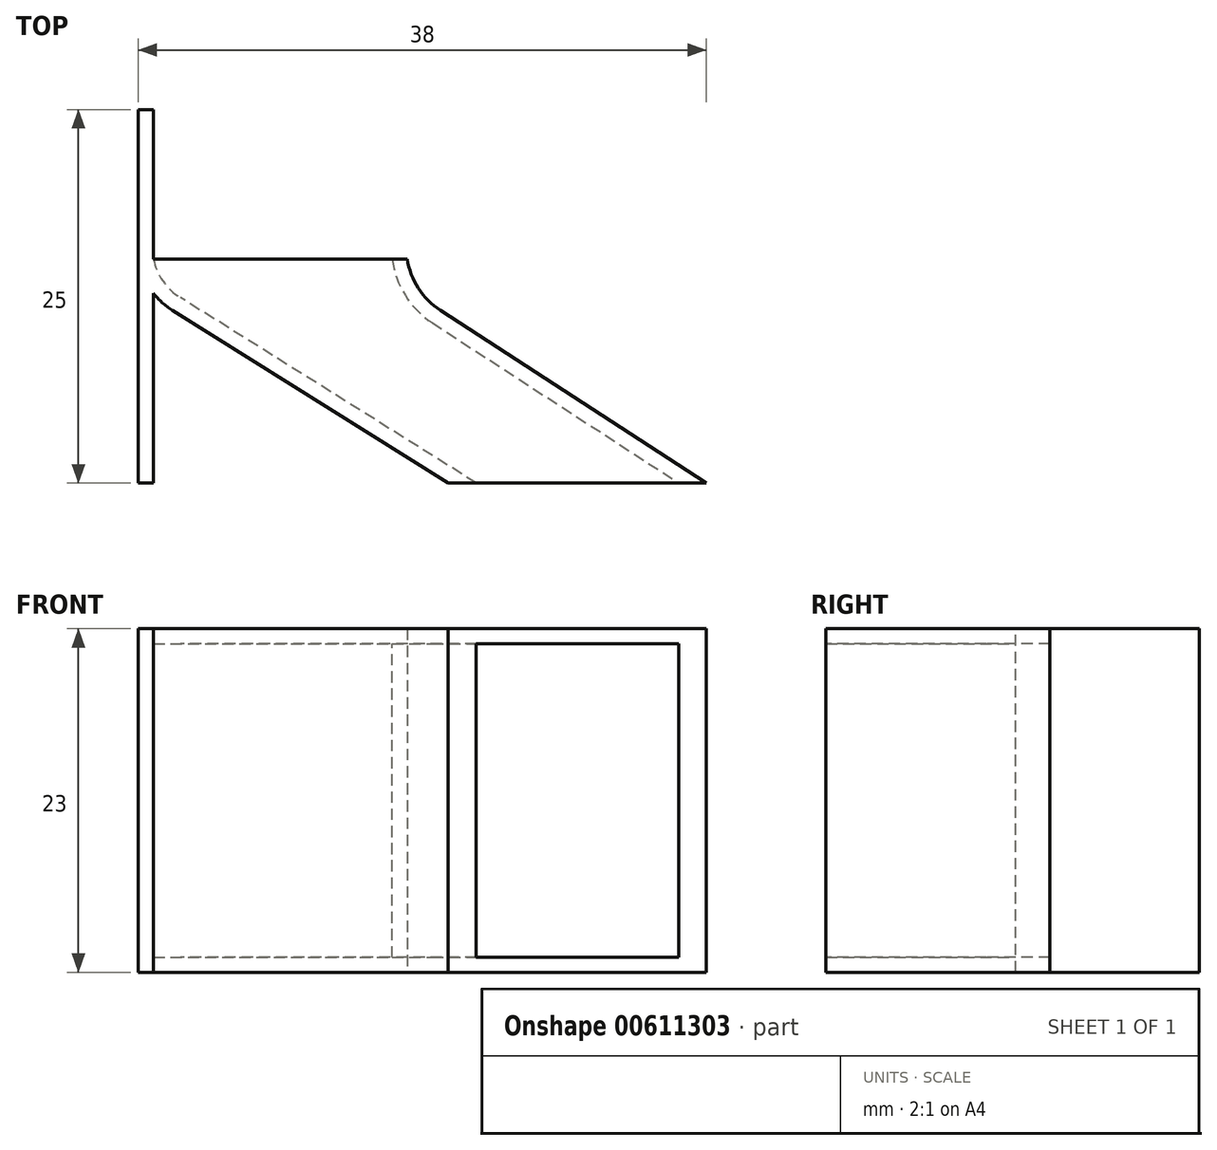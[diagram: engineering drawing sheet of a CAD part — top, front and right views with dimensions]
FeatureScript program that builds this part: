
annotation { "Feature Type Name" : "Feature", "Feature Type Description" : "" }
export const myFeature = defineFeature(function(context is Context, id is Id, definition is map)
    precondition{}
    {
        {
            var Q0;
            Q0=qCreatedBy(makeId("Top.planeOp"),FACE);
            var sketch = newSketch(context, id + "F0", { "sketchPlane" : qUnion([Q0])});
            skLineSegment(sketch, "E0.bottom", {"start": v(0, 0) * mm, "end": v(18, 0) * mm});
            skLineSegment(sketch, "E0.top", {"start": v(0, 2) * mm, "end": v(18, 2) * mm, "construction": true});
            skLineSegment(sketch, "E0.left", {"start": v(0, 0) * mm, "end": v(0, 2) * mm, "construction": true});
            skLineSegment(sketch, "E0.right", {"start": v(18, 0) * mm, "end": v(18, 2) * mm, "construction": true});
            skLineSegment(sketch, "E1.bottom", {"start": v(0, 0) * mm, "end": v(38, 0) * mm, "construction": true});
            skLineSegment(sketch, "E1.top", {"start": v(0, -13) * mm, "end": v(38, -13) * mm, "construction": true});
            skLineSegment(sketch, "E1.left", {"start": v(0, 0) * mm, "end": v(0, -13) * mm, "construction": true});
            skLineSegment(sketch, "E1.right", {"start": v(38, 0) * mm, "end": v(38, -13) * mm, "construction": true});
            skLineSegment(sketch, "E2", {"start": v(0, 2) * mm, "end": v(18, 2) * mm});
            skLineSegment(sketch, "E3", {"start": v(18, 0) * mm, "end": v(38, -13) * mm});
            skLineSegment(sketch, "E4", {"start": v(20.74, -13) * mm, "end": v(0, 0) * mm});
            skLineSegment(sketch, "E5", {"start": v(0, 2) * mm, "end": v(0, 0) * mm});
            skLineSegment(sketch, "E6", {"start": v(18, 2) * mm, "end": v(18, 0) * mm});
            skLineSegment(sketch, "E7", {"start": v(38, -13) * mm, "end": v(20.74, -13) * mm});
            skSolve(sketch);
        }
        {
            var Q0;
            Q0 = qSketchRegion(id + "F0", true);
            extrude(context, id + "F1", {"entities" : qUnion([Q0]), "depth" : 23 * mm, "offsetDistance" : 25 * mm});
        }
        {
            var Q0;
            Q0=makeQuery(id+"F1.opExtrude","SWEPT_EDGE",EDGE,{"disambiguationData":[OSD([sQuery(id+"F0.wireOp",EDGE,"E0.bottom"),sQuery(id+"F0.wireOp",EDGE,"E4"),sQuery(id+"F0.wireOp",EDGE,"E5")])]});
            fillet(context, id + "F2", {"entities" : qUnion([Q0]), "radius" : 5 * mm, "tangentPropagation" : true, "allowEdgeOverflow" : false});
        }
        {
            var Q0;
            Q0=makeQuery(id+"F1.opExtrude","SWEPT_EDGE",EDGE,{"disambiguationData":[OSD([sQuery(id+"F0.wireOp",EDGE,"E0.bottom"),sQuery(id+"F0.wireOp",EDGE,"E3"),sQuery(id+"F0.wireOp",EDGE,"E6")])]});
            fillet(context, id + "F3", {"entities" : qUnion([Q0]), "radius" : 5 * mm, "tangentPropagation" : true, "allowEdgeOverflow" : false});
        }
        {
            var Q0;
            Q0=makeQuery(id+"F1.opExtrude","SWEPT_FACE",FACE,{"disambiguationData":[OSD([sQuery(id+"F0.wireOp",EDGE,"E2")])]});
            var Q1;
            Q1=makeQuery(id+"F1.opExtrude","SWEPT_FACE",FACE,{"disambiguationData":[OSD([sQuery(id+"F0.wireOp",EDGE,"E7")])]});
            shell(context, id + "F4", {"entities" : qUnion([Q0, Q1]), "thickness" : 1 * mm});
        }
        {
            var Q0;
            Q0=makeQuery(id+"F1.opExtrude","SWEPT_FACE",FACE,{"disambiguationData":[OSD([sQuery(id+"F0.wireOp",EDGE,"E2")])]});
            var sketch = newSketch(context, id + "F5", { "sketchPlane" : qUnion([Q0])});
            skLineSegment(sketch, "E8.bottom", {"start": v(0, 23) * mm, "end": v(-1.02, 23) * mm});
            skLineSegment(sketch, "E8.top", {"start": v(0, 0) * mm, "end": v(-1.02, 0) * mm});
            skLineSegment(sketch, "E8.left", {"start": v(0, 23) * mm, "end": v(0, 0) * mm});
            skLineSegment(sketch, "E8.right", {"start": v(-1.02, 23) * mm, "end": v(-1.02, 0) * mm});
            skSolve(sketch);
        }
        {
            var Q0;
            Q0 = qSketchRegion(id + "F5", true);
            extrude(context, id + "F6", {"entities" : qUnion([Q0]), "operationType" : NewBodyOperationType.ADD, "depth" : 10 * mm, "offsetDistance" : 25 * mm, "hasSecondDirection" : true, "secondDirectionOppositeDirection" : true, "secondDirectionDepth" : 15 * mm});
        }
    });
